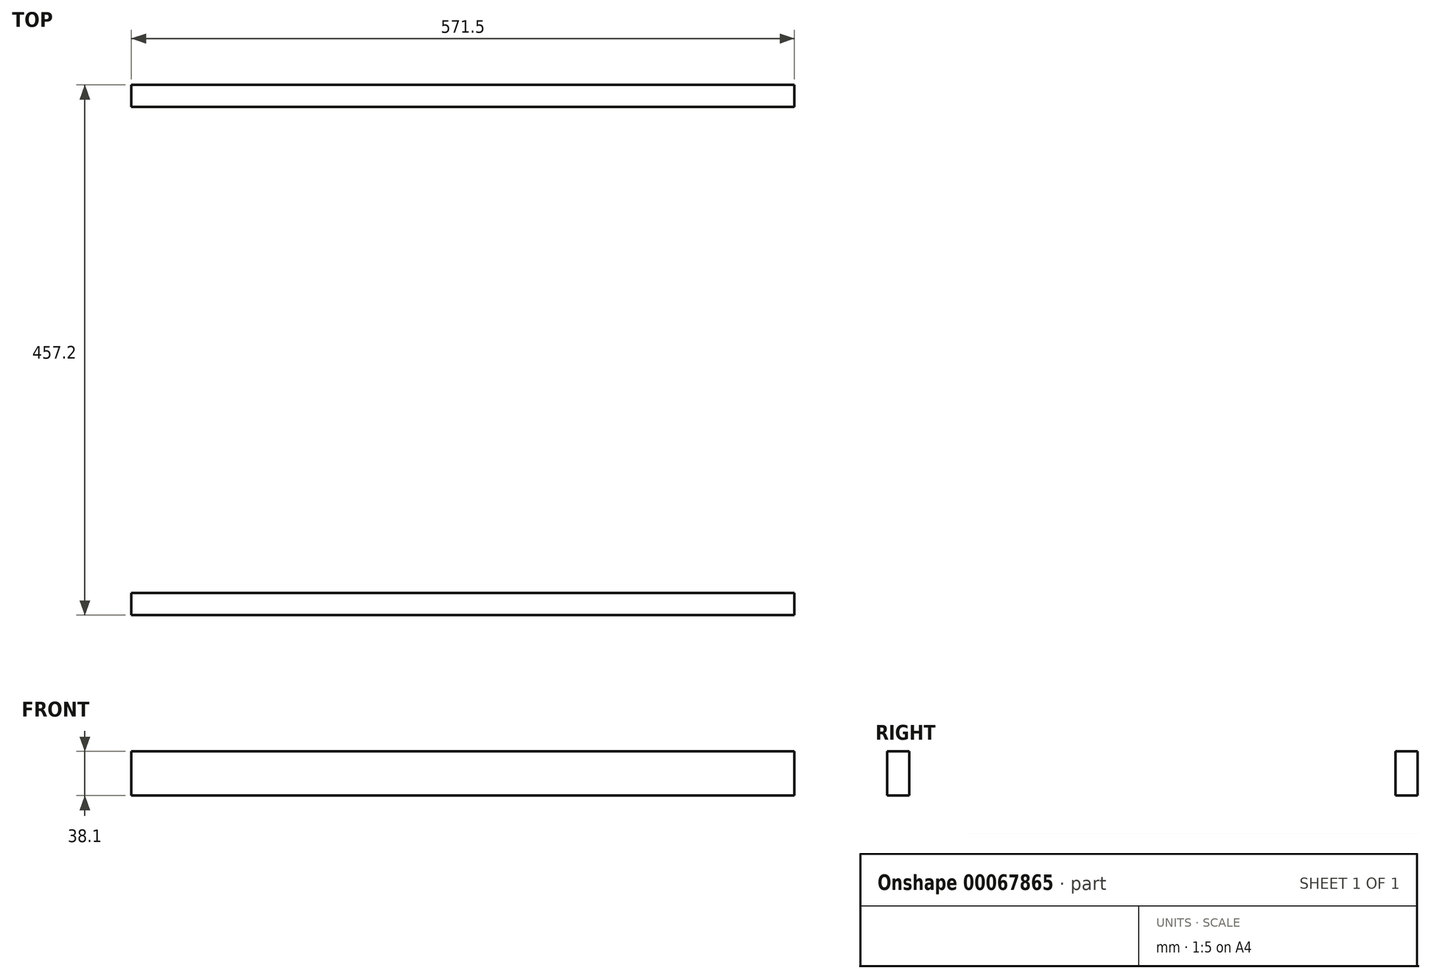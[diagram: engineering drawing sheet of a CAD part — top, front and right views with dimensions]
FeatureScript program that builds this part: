
annotation { "Feature Type Name" : "Feature", "Feature Type Description" : "" }
export const myFeature = defineFeature(function(context is Context, id is Id, definition is map)
    precondition{}
    {
        {
            var Q0;
            Q0=qCreatedBy(makeId("Top.planeOp"),FACE);
            var sketch = newSketch(context, id + "F0", { "sketchPlane" : qUnion([Q0])});
            skLineSegment(sketch, "E0", {"start": v(-304.8, 0) * mm, "end": v(304.8, 0) * mm, "construction": true});
            skLineSegment(sketch, "E1", {"start": v(0, 228.6) * mm, "end": v(0, -228.6) * mm, "construction": true});
            skLineSegment(sketch, "E2.bottom", {"start": v(-285.75, -228.6) * mm, "end": v(285.75, -228.6) * mm});
            skLineSegment(sketch, "E2.top", {"start": v(-285.75, -209.55) * mm, "end": v(285.75, -209.55) * mm});
            skLineSegment(sketch, "E2.left", {"start": v(-285.75, -228.6) * mm, "end": v(-285.75, -209.55) * mm});
            skLineSegment(sketch, "E2.right", {"start": v(285.75, -228.6) * mm, "end": v(285.75, -209.55) * mm});
            skLineSegment(sketch, "E3.bottom", {"start": v(-285.75, 228.6) * mm, "end": v(285.75, 228.6) * mm});
            skLineSegment(sketch, "E3.top", {"start": v(-285.75, 209.55) * mm, "end": v(285.75, 209.55) * mm});
            skLineSegment(sketch, "E3.left", {"start": v(-285.75, 228.6) * mm, "end": v(-285.75, 209.55) * mm});
            skLineSegment(sketch, "E3.right", {"start": v(285.75, 228.6) * mm, "end": v(285.75, 209.55) * mm});
            skSolve(sketch);
        }
        {
            var Q0;
            Q0=makeQuery(id+"F0.imprint","IMPRINT",FACE,{"disambiguationData":[TD([[makeQuery(id+"F0.imprint","IMPRINT",EDGE,{"derivedFrom":sQuery(id+"F0.wireOp",EDGE,"E3.bottom")}),-1.0]])]});
            var Q1;
            Q1=makeQuery(id+"F0.imprint","IMPRINT",FACE,{"disambiguationData":[TD([[makeQuery(id+"F0.imprint","IMPRINT",EDGE,{"derivedFrom":sQuery(id+"F0.wireOp",EDGE,"E2.bottom")}),1.0]])]});
            extrude(context, id + "F1", {"entities" : qUnion([Q0, Q1]), "depth" : 38.1 * mm});
        }
        {
            var Q0;
            Q0=makeQuery(id+"F1.opExtrude","CAP_FACE",FACE,{"disambiguationData":[OSD([sQuery(id+"F0.wireOp",EDGE,"E3.bottom"),sQuery(id+"F0.wireOp",EDGE,"E3.top"),sQuery(id+"F0.wireOp",EDGE,"E3.left"),sQuery(id+"F0.wireOp",EDGE,"E3.right")])],"isStart":false});
            cPlane(context, id + "F2", {"entities" : qUnion([Q0]), "cplaneType" : CPlaneType.OFFSET, "offset" : 19.05 * mm, "width" : 152.4 * mm, "height" : 152.4 * mm});
        }
    });
